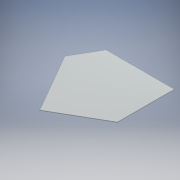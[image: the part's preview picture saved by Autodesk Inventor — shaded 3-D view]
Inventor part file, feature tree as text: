
AUTODESK INVENTOR PART (.ipt)
format: ipt  version: 2016 SP1 (Build 200210100, 210)  size: 124,928 bytes
history: native  units: mm
features: reference x3, extrude x1, sketch x1
ambient origin geometry x8: Origin, YZ Plane, XZ Plane, XY Plane, X Axis, Y Axis, Z Axis, Center Point
bodies: Solid1 (feature_tree)
feature tree (5):
  extrude  "Extrusion1"  [1 undecoded]
  sketch  "Sketch1"  dims[d0=1.5mm d1=0.0mm]
  reference  "Reference1"
  reference  "Reference2"
  reference  "Reference3"
note: 1 required parameter value undecoded (feature->parameter linkage not recoverable at this tier; creation-order binding heuristic only, values carry confidence <= 0.55)
